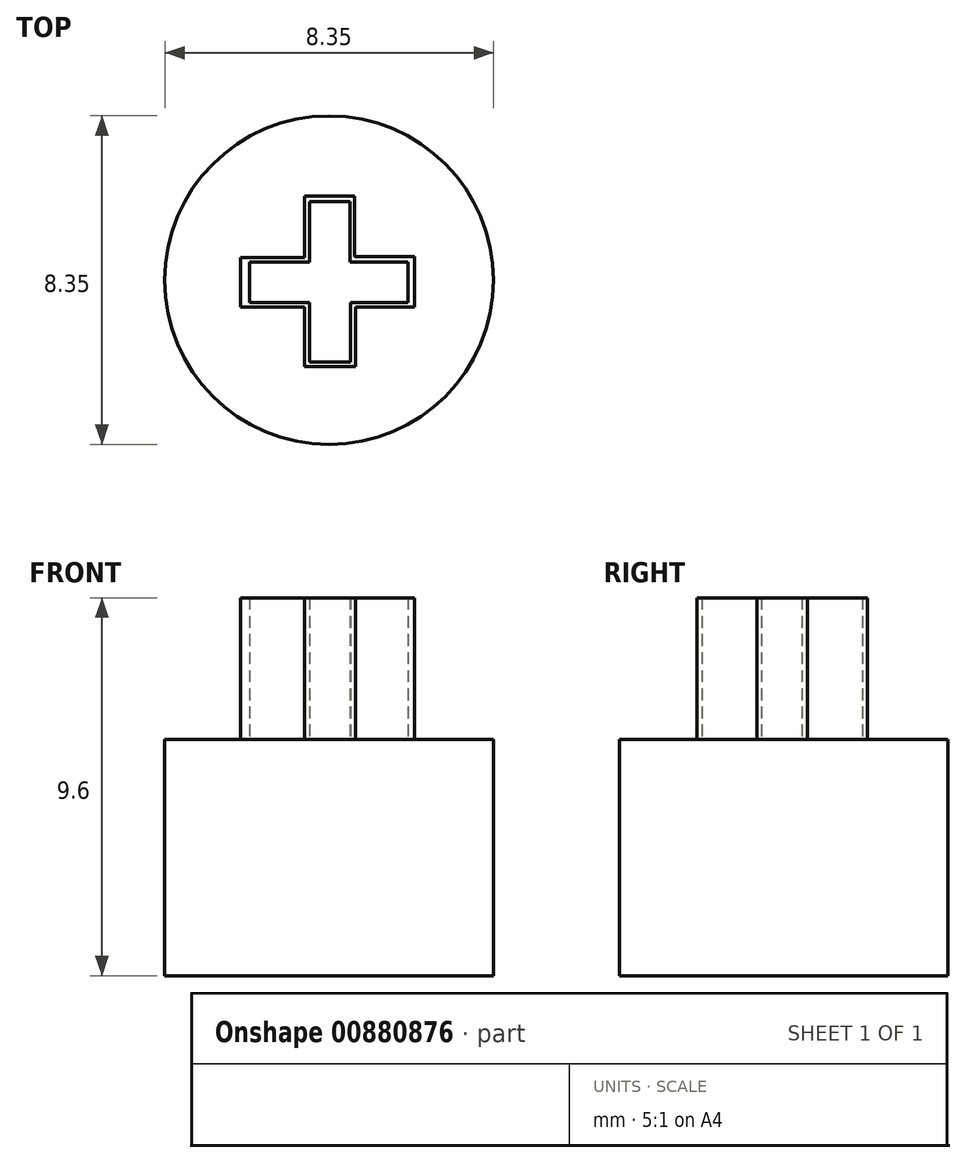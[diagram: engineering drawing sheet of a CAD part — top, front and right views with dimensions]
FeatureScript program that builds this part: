
annotation { "Feature Type Name" : "Feature", "Feature Type Description" : "" }
export const myFeature = defineFeature(function(context is Context, id is Id, definition is map)
    precondition{}
    {
        {
            var Q0;
            Q0=qCreatedBy(makeId("Top.planeOp"),FACE);
            var sketch = newSketch(context, id + "F0", { "sketchPlane" : qUnion([Q0])});
            skArc(sketch, "E0", {"start": v(-16.33, -3.7) * mm, "mid": v(-16.04, -4.5) * mm, "end": v(-15.3, -4.9) * mm});
            skLineSegment(sketch, "E1", {"start": v(-15.3, -4.9) * mm, "end": v(0.7, -4.9) * mm});
            skArc(sketch, "E2", {"start": v(0.7, -4.9) * mm, "mid": v(1.53, -4.58) * mm, "end": v(1.97, -3.81) * mm});
            skLineSegment(sketch, "E3", {"start": v(1.97, -3.81) * mm, "end": v(1.97, 12.15) * mm});
            skArc(sketch, "E4", {"start": v(1.97, 12.15) * mm, "mid": v(1.64, 13) * mm, "end": v(0.83, 13.4) * mm});
            skLineSegment(sketch, "E5", {"start": v(0.83, 13.4) * mm, "end": v(-15.1, 13.4) * mm});
            skArc(sketch, "E6", {"start": v(-15.1, 13.4) * mm, "mid": v(-15.95, 13.07) * mm, "end": v(-16.33, 12.24) * mm});
            skLineSegment(sketch, "E7", {"start": v(-16.33, -3.7) * mm, "end": v(-16.33, 12.24) * mm});
            skCircle(sketch, "E8", {"center": v(-7.17, 4.25) * mm, "radius": 2.79 * mm});
            skPoint(sketch, "E8.first.point", {"position": v(-9.1, 6.26) * mm});
            skPoint(sketch, "E8.second.point", {"position": v(-5.32, 2.17) * mm});
            skPoint(sketch, "E8.third.point", {"position": v(-4.95, 5.93) * mm});
            skLineSegment(sketch, "E9", {"start": v(-7.68, 6.22) * mm, "end": v(-7.68, 4.7) * mm});
            skLineSegment(sketch, "E10", {"start": v(-7.68, 4.7) * mm, "end": v(-9.2, 4.7) * mm});
            skLineSegment(sketch, "E11", {"start": v(-9.2, 4.7) * mm, "end": v(-9.2, 3.68) * mm});
            skLineSegment(sketch, "E12", {"start": v(-9.2, 3.68) * mm, "end": v(-7.68, 3.68) * mm});
            skLineSegment(sketch, "E13", {"start": v(-7.68, 3.68) * mm, "end": v(-7.68, 2.17) * mm});
            skLineSegment(sketch, "E14", {"start": v(-7.68, 2.17) * mm, "end": v(-6.64, 2.17) * mm});
            skLineSegment(sketch, "E15", {"start": v(-6.64, 2.17) * mm, "end": v(-6.64, 3.68) * mm});
            skLineSegment(sketch, "E16", {"start": v(-6.64, 3.68) * mm, "end": v(-5.17, 3.68) * mm});
            skLineSegment(sketch, "E17", {"start": v(-5.17, 3.68) * mm, "end": v(-5.17, 4.7) * mm});
            skLineSegment(sketch, "E18", {"start": v(-5.17, 4.7) * mm, "end": v(-6.64, 4.7) * mm});
            skLineSegment(sketch, "E19", {"start": v(-6.64, 4.7) * mm, "end": v(-6.64, 6.24) * mm});
            skLineSegment(sketch, "E20", {"start": v(-6.64, 6.24) * mm, "end": v(-7.68, 6.24) * mm});
            skLineSegment(sketch, "E21", {"start": v(-7.68, 6.24) * mm, "end": v(-7.68, 6.22) * mm});
            skLineSegment(sketch, "E22", {"start": v(-7.8, 3.4) * mm, "end": v(-7.8, 2.04) * mm});
            skLineSegment(sketch, "E23", {"start": v(-7.8, 2.04) * mm, "end": v(-6.51, 2.04) * mm});
            skLineSegment(sketch, "E24", {"start": v(-6.51, 2.04) * mm, "end": v(-6.51, 3.57) * mm});
            skLineSegment(sketch, "E25", {"start": v(-6.51, 3.57) * mm, "end": v(-5, 3.57) * mm});
            skLineSegment(sketch, "E26", {"start": v(-5, 3.57) * mm, "end": v(-5, 4.85) * mm});
            skLineSegment(sketch, "E27", {"start": v(-5, 4.85) * mm, "end": v(-6.53, 4.85) * mm});
            skLineSegment(sketch, "E28", {"start": v(-6.53, 4.85) * mm, "end": v(-6.53, 6.37) * mm});
            skLineSegment(sketch, "E29", {"start": v(-6.53, 6.37) * mm, "end": v(-7.8, 6.37) * mm});
            skLineSegment(sketch, "E30", {"start": v(-7.8, 6.37) * mm, "end": v(-7.8, 4.82) * mm});
            skLineSegment(sketch, "E31", {"start": v(-7.8, 4.82) * mm, "end": v(-9.42, 4.82) * mm});
            skLineSegment(sketch, "E32", {"start": v(-9.42, 4.82) * mm, "end": v(-9.42, 3.57) * mm});
            skLineSegment(sketch, "E33", {"start": v(-9.42, 3.57) * mm, "end": v(-7.8, 3.57) * mm});
            skLineSegment(sketch, "E34", {"start": v(-7.8, 3.4) * mm, "end": v(-7.8, 3.57) * mm});
            skSolve(sketch);
        }
        {
            var Q0;
            Q0=makeQuery(id+"F0.imprint","IMPRINT",FACE,{"disambiguationData":[TD([[makeQuery(id+"F0.imprint","IMPRINT",EDGE,{"derivedFrom":sQuery(id+"F0.wireOp",EDGE,"E9")}),-1.0]])]});
            extrude(context, id + "F1", {"entities" : qUnion([Q0]), "depth" : 3.6 * mm, "offsetDistance" : 25 * mm});
        }
        {
            var Q0;
            Q0=makeQuery(id+"F1.opExtrude","CAP_FACE",FACE,{"disambiguationData":[OSD([sQuery(id+"F0.wireOp",EDGE,"E9"),sQuery(id+"F0.wireOp",EDGE,"E10"),sQuery(id+"F0.wireOp",EDGE,"E11"),sQuery(id+"F0.wireOp",EDGE,"E12"),sQuery(id+"F0.wireOp",EDGE,"E13"),sQuery(id+"F0.wireOp",EDGE,"E14"),sQuery(id+"F0.wireOp",EDGE,"E15"),sQuery(id+"F0.wireOp",EDGE,"E16"),sQuery(id+"F0.wireOp",EDGE,"E17"),sQuery(id+"F0.wireOp",EDGE,"E18"),sQuery(id+"F0.wireOp",EDGE,"E19"),sQuery(id+"F0.wireOp",EDGE,"E20"),sQuery(id+"F0.wireOp",EDGE,"E21"),sQuery(id+"F0.wireOp",EDGE,"E22"),sQuery(id+"F0.wireOp",EDGE,"E23"),sQuery(id+"F0.wireOp",EDGE,"E24"),sQuery(id+"F0.wireOp",EDGE,"E25"),sQuery(id+"F0.wireOp",EDGE,"E26"),sQuery(id+"F0.wireOp",EDGE,"E27"),sQuery(id+"F0.wireOp",EDGE,"E28"),sQuery(id+"F0.wireOp",EDGE,"E29"),sQuery(id+"F0.wireOp",EDGE,"E30"),sQuery(id+"F0.wireOp",EDGE,"E31"),sQuery(id+"F0.wireOp",EDGE,"E32"),sQuery(id+"F0.wireOp",EDGE,"E33"),sQuery(id+"F0.wireOp",EDGE,"E34")])],"isStart":true});
            var sketch = newSketch(context, id + "F2", { "sketchPlane" : qUnion([Q0])});
            skCircle(sketch, "E35", {"center": v(-7.18, -4.24) * mm, "radius": 4.18 * mm});
            skSolve(sketch);
        }
        {
            var Q0;
            Q0=qSketchRegion(id+"F2",true);
            extrude(context, id + "F3", {"entities" : qUnion([Q0]), "operationType" : NewBodyOperationType.ADD, "depth" : 6 * mm, "offsetDistance" : 25 * mm});
        }
        {
            var Q0;
            Q0=makeQuery(id+"F3.opExtrude","CAP_FACE",FACE,{"disambiguationData":[OSD([sQuery(id+"F2.wireOp",EDGE,"E35")])],"isStart":false});
            var sketch = newSketch(context, id + "F4", { "sketchPlane" : qUnion([Q0])});
            skText(sketch, "E36", { "text": ">\n", "fontName": "OpenSans-Regular.ttf"});
            const initialGuessF4  = {"E36": [-0.00885, -0.00628, 1, 0, 0.00381]};
            skSetInitialGuess(sketch, initialGuessF4);
            skSolve(sketch);
        }
        {
            var Q0;
            Q0 = qSketchRegion(id + "F4", true);
            extrude(context, id + "F5", {"entities" : qUnion([Q0]), "operationType" : NewBodyOperationType.ADD, "depth" : -.5 * mm, "offsetDistance" : 25 * mm});
        }
    });
